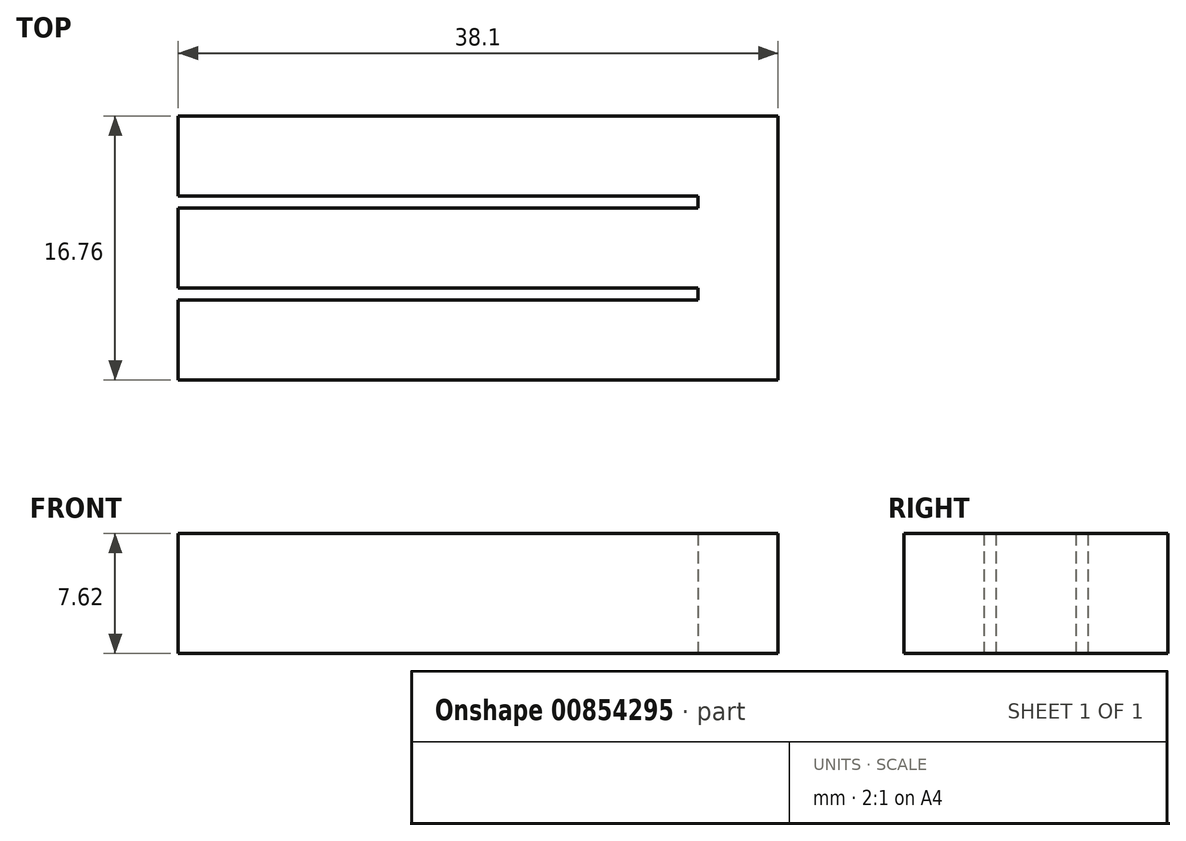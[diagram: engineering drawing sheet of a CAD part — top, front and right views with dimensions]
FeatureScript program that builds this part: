
annotation { "Feature Type Name" : "Feature", "Feature Type Description" : "" }
export const myFeature = defineFeature(function(context is Context, id is Id, definition is map)
    precondition{}
    {
        {
            var Q0;
            Q0=qCreatedBy(makeId("Top.planeOp"),FACE);
            var sketch = newSketch(context, id + "F0", { "sketchPlane" : qUnion([Q0])});
            skLineSegment(sketch, "E0", {"start": v(0, 0) * mm, "end": v(0, 16.76) * mm});
            skLineSegment(sketch, "E1", {"start": v(0, 16.76) * mm, "end": v(-38.1, 16.76) * mm});
            skLineSegment(sketch, "E2", {"start": v(-38.1, 16.76) * mm, "end": v(-38.1, 11.68) * mm});
            skLineSegment(sketch, "E3", {"start": v(-38.1, 11.68) * mm, "end": v(-5.08, 11.68) * mm});
            skLineSegment(sketch, "E4", {"start": v(-5.08, 10.92) * mm, "end": v(-38.1, 10.92) * mm});
            skLineSegment(sketch, "E5", {"start": v(-38.1, 10.92) * mm, "end": v(-38.1, 5.84) * mm});
            skLineSegment(sketch, "E6", {"start": v(-38.1, 5.08) * mm, "end": v(-5.08, 5.08) * mm});
            skLineSegment(sketch, "E7", {"start": v(-5.08, 5.84) * mm, "end": v(-5.08, 5.08) * mm});
            skLineSegment(sketch, "E8", {"start": v(-5.08, 5.84) * mm, "end": v(-38.1, 5.84) * mm});
            skLineSegment(sketch, "E9", {"start": v(-38.1, 5.08) * mm, "end": v(-38.1, 0) * mm});
            skLineSegment(sketch, "E10", {"start": v(-38.1, 0) * mm, "end": v(0, 0) * mm});
            skLineSegment(sketch, "E11", {"start": v(-5.08, 11.68) * mm, "end": v(-5.08, 10.92) * mm});
            skSolve(sketch);
        }
        {
            var Q0;
            Q0=makeQuery(id+"F0.imprint","IMPRINT",FACE,{"disambiguationData":[TD([[makeQuery(id+"F0.imprint","IMPRINT",EDGE,{"derivedFrom":sQuery(id+"F0.wireOp",EDGE,"E1")}),1.0]])]});
            extrude(context, id + "F1", {"entities" : qUnion([Q0]), "depth" : 7.62 * mm, "offsetDistance" : 25.4 * mm});
        }
    });
